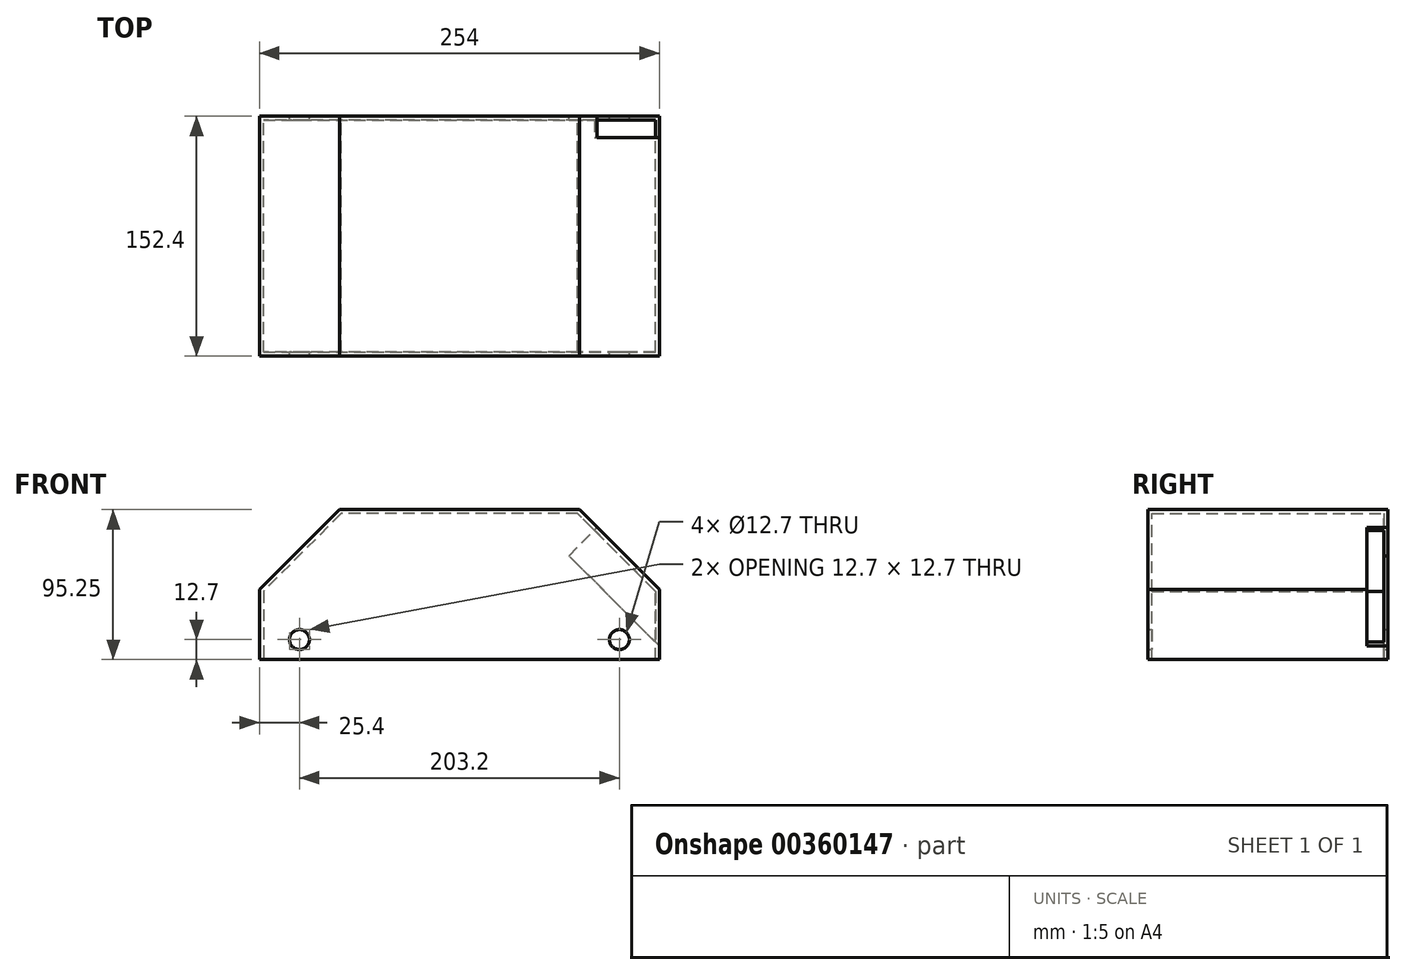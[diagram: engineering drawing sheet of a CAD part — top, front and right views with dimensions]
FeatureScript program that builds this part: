
annotation { "Feature Type Name" : "Feature", "Feature Type Description" : "" }
export const myFeature = defineFeature(function(context is Context, id is Id, definition is map)
    precondition{}
    {
        {
            var Q0;
            Q0=qCreatedBy(makeId("Front.planeOp"),FACE);
            var sketch = newSketch(context, id + "F0", { "sketchPlane" : qUnion([Q0])});
            skLineSegment(sketch, "E0", {"start": v(-127, 44.45) * mm, "end": v(-127, 0) * mm});
            skLineSegment(sketch, "E1", {"start": v(-127, 0) * mm, "end": v(127, 0) * mm});
            skLineSegment(sketch, "E2", {"start": v(127, 0) * mm, "end": v(127, 44.45) * mm});
            skLineSegment(sketch, "E3", {"start": v(127, 44.45) * mm, "end": v(76.2, 95.25) * mm});
            skLineSegment(sketch, "E4", {"start": v(76.2, 95.25) * mm, "end": v(-76.2, 95.25) * mm});
            skLineSegment(sketch, "E5", {"start": v(-76.2, 95.25) * mm, "end": v(-127, 44.45) * mm});
            skCircle(sketch, "E6", {"center": v(-101.6, 12.7) * mm, "radius": 6.35 * mm});
            skCircle(sketch, "E7", {"center": v(101.6, 12.7) * mm, "radius": 6.35 * mm});
            skSolve(sketch);
        }
        {
            var Q0;
            Q0=makeQuery(id+"F0.imprint","IMPRINT",FACE,{"disambiguationData":[TD([[makeQuery(id+"F0.imprint","IMPRINT",EDGE,{"derivedFrom":sQuery(id+"F0.wireOp",EDGE,"E0")}),1.0]])]});
            extrude(context, id + "F1", {"entities" : qUnion([Q0]), "depth" : 152.4 * mm});
        }
        {
            var Q0;
            Q0=makeQuery(id+"F1.opExtrude","SWEPT_FACE",FACE,{"disambiguationData":[OSD([sQuery(id+"F0.wireOp",EDGE,"E1")])]});
            shell(context, id + "F2", {"entities" : qUnion([Q0]), "thickness" : 2.54 * mm});
        }
        {
            var Q0;
            Q0=makeQuery(id+"F1.opExtrude","SWEPT_FACE",FACE,{"disambiguationData":[OSD([sQuery(id+"F0.wireOp",EDGE,"E1")])]});
            var sketch = newSketch(context, id + "F3", { "sketchPlane" : qUnion([Q0])});
            skLineSegment(sketch, "E8.bottom", {"start": v(-124.46, 2.54) * mm, "end": v(124.46, 2.54) * mm});
            skLineSegment(sketch, "E8.top", {"start": v(-124.46, 149.86) * mm, "end": v(124.46, 149.86) * mm});
            skLineSegment(sketch, "E8.left", {"start": v(-124.46, 2.54) * mm, "end": v(-124.46, 149.86) * mm});
            skLineSegment(sketch, "E8.right", {"start": v(124.46, 2.54) * mm, "end": v(124.46, 149.86) * mm});
            skSolve(sketch);
        }
        {
            var Q0;
            Q0 = qSketchRegion(id + "F3", true);
            extrude(context, id + "F4", {"entities" : qUnion([Q0]), "operationType" : NewBodyOperationType.REMOVE, "oppositeDirection" : true, "depth" : 25.4 * mm});
        }
        {
            var Q0;
            Q0=makeQuery(id+"F1.opExtrude","SWEPT_FACE",FACE,{"disambiguationData":[OSD([sQuery(id+"F0.wireOp",EDGE,"E3")])]});
            var sketch = newSketch(context, id + "F5", { "sketchPlane" : qUnion([Q0])});
            skLineSegment(sketch, "E9.bottom", {"start": v(-13.47, -149.86) * mm, "end": v(58.37, -149.86) * mm});
            skLineSegment(sketch, "E9.top", {"start": v(-13.47, -2.54) * mm, "end": v(58.37, -2.54) * mm});
            skLineSegment(sketch, "E9.left", {"start": v(-13.47, -149.86) * mm, "end": v(-13.47, -2.54) * mm});
            skLineSegment(sketch, "E9.right", {"start": v(58.37, -149.86) * mm, "end": v(58.37, -2.54) * mm});
            skSolve(sketch);
        }
        {
            var Q0;
            Q0 = qSketchRegion(id + "F5", true);
            extrude(context, id + "F6", {"entities" : qUnion([Q0]), "operationType" : NewBodyOperationType.REMOVE, "oppositeDirection" : true, "depth" : 25.4 * mm});
        }
    });
